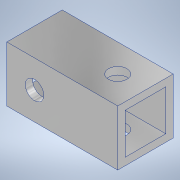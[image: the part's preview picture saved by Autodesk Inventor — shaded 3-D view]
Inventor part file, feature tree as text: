
AUTODESK INVENTOR PART (.ipt)
format: ipt  version: 2020.3 (Build 243373000, 373)  size: 121,344 bytes
history: native  units: mm
features: sketch x3, hole x2, other x1, extrude x1
ambient origin geometry x8: Origin, YZ Plane, XZ Plane, XY Plane, X Axis, Y Axis, Z Axis, Center Point
bodies: Body1 (feature_tree)
feature tree (7):
  other  "ソリッド1"
  extrude  "押し出し1"  Depth=9.0mm
  hole  "穴1"  [1 undecoded]
  hole  "穴2"  [1 undecoded]
  sketch  "スケッチ1"
  sketch  "スケッチ2"
  sketch  "スケッチ3"
note: 2 required parameter values undecoded (feature->parameter linkage not recoverable at this tier; creation-order binding heuristic only, values carry confidence <= 0.55)
